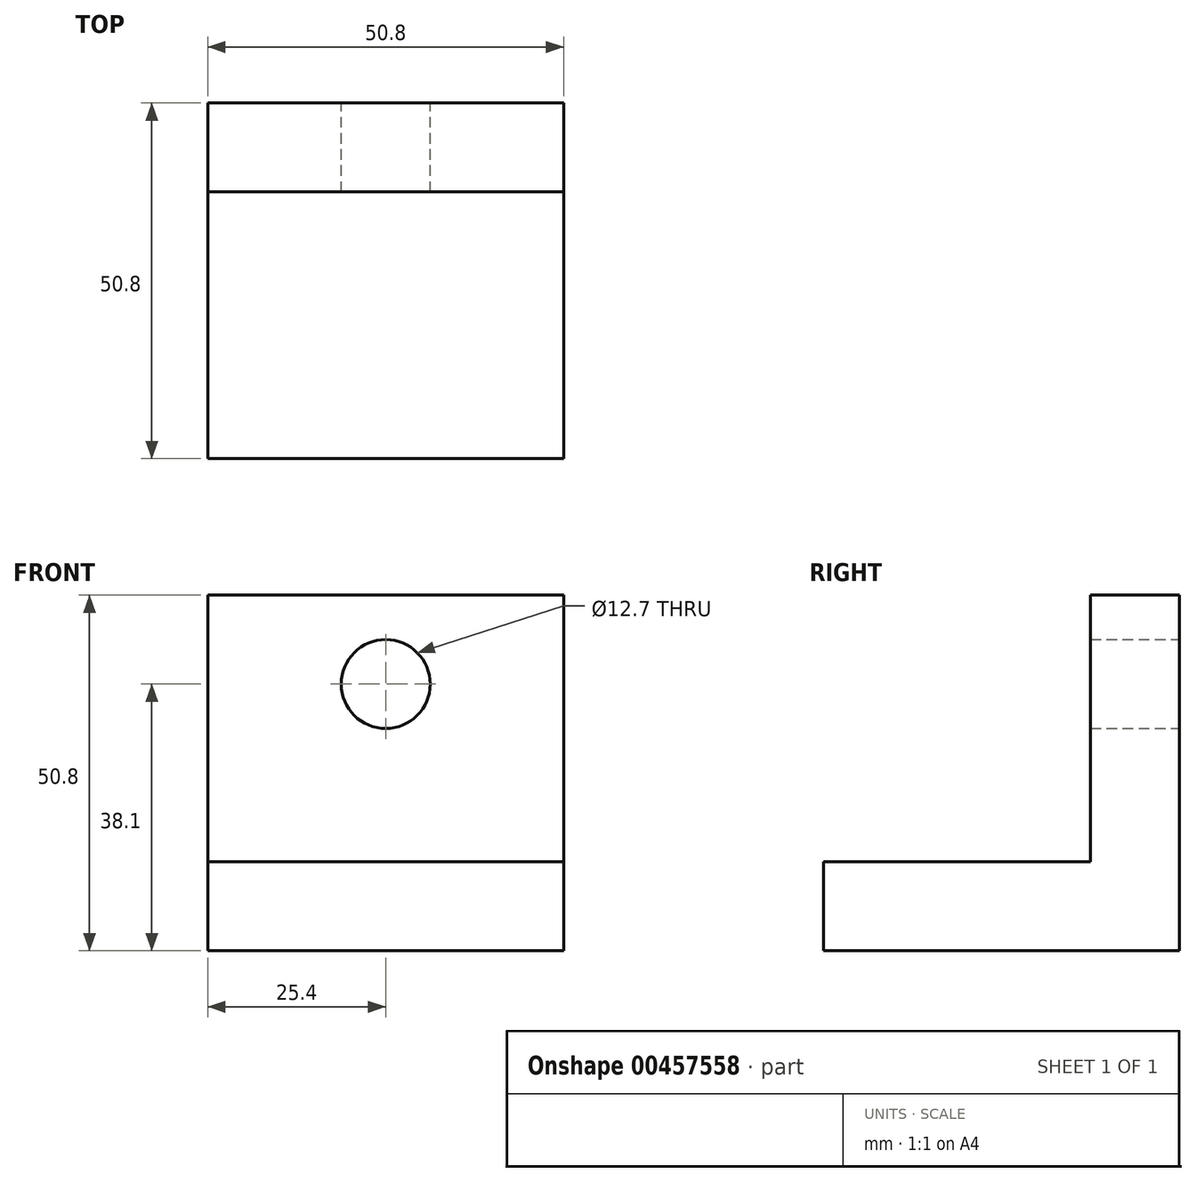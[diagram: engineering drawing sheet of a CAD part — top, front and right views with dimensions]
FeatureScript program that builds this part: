
annotation { "Feature Type Name" : "Feature", "Feature Type Description" : "" }
export const myFeature = defineFeature(function(context is Context, id is Id, definition is map)
    precondition{}
    {
        {
            var Q0;
            Q0=qCreatedBy(makeId("Front.planeOp"),FACE);
            var sketch = newSketch(context, id + "F0", { "sketchPlane" : qUnion([Q0])});
            skLineSegment(sketch, "E0.bottom", {"start": v(25.4, 25.4) * mm, "end": v(-25.4, 25.4) * mm});
            skLineSegment(sketch, "E0.top", {"start": v(25.4, -25.4) * mm, "end": v(-25.4, -25.4) * mm});
            skLineSegment(sketch, "E0.left", {"start": v(25.4, 25.4) * mm, "end": v(25.4, -25.4) * mm});
            skLineSegment(sketch, "E0.right", {"start": v(-25.4, 25.4) * mm, "end": v(-25.4, -25.4) * mm});
            skPoint(sketch, "E0.middle", {"position": v(0, 0) * mm});
            skCircle(sketch, "E1", {"center": v(0, 12.7) * mm, "radius": 6.35 * mm});
            skPoint(sketch, "E1.centerSnap0", {"position": v(0, 25.4) * mm});
            skSolve(sketch);
        }
        {
            var Q0;
            Q0=makeQuery(id+"F0.imprint","IMPRINT",FACE,{"disambiguationData":[TD([[makeQuery(id+"F0.imprint","IMPRINT",EDGE,{"derivedFrom":sQuery(id+"F0.wireOp",EDGE,"E0.bottom")}),1.0]])]});
            extrude(context, id + "F1", {"entities" : qUnion([Q0]), "depth" : 12.7 * mm});
        }
        {
            var Q0;
            Q0=makeQuery(id+"F1.opExtrude","CAP_FACE",FACE,{"disambiguationData":[OSD([sQuery(id+"F0.wireOp",EDGE,"E0.bottom"),sQuery(id+"F0.wireOp",EDGE,"E0.top"),sQuery(id+"F0.wireOp",EDGE,"E0.left"),sQuery(id+"F0.wireOp",EDGE,"E0.right"),sQuery(id+"F0.wireOp",EDGE,"E1")])],"isStart":false});
            var sketch = newSketch(context, id + "F2", { "sketchPlane" : qUnion([Q0])});
            skLineSegment(sketch, "E2.bottom", {"start": v(-25.4, -25.4) * mm, "end": v(25.4, -25.4) * mm});
            skLineSegment(sketch, "E2.top", {"start": v(-25.4, -12.7) * mm, "end": v(25.4, -12.7) * mm});
            skLineSegment(sketch, "E2.left", {"start": v(-25.4, -25.4) * mm, "end": v(-25.4, -12.7) * mm});
            skLineSegment(sketch, "E2.right", {"start": v(25.4, -25.4) * mm, "end": v(25.4, -12.7) * mm});
            skSolve(sketch);
        }
        {
            var Q0;
            Q0=makeQuery(id+"F2.imprint","IMPRINT",FACE,{"disambiguationData":[TD([[makeQuery(id+"F2.imprint","IMPRINT",EDGE,{"derivedFrom":sQuery(id+"F2.wireOp",EDGE,"E2.bottom")}),-1.0]])]});
            extrude(context, id + "F3", {"entities" : qUnion([Q0]), "operationType" : NewBodyOperationType.ADD, "depth" : 38.1 * mm});
        }
    });
